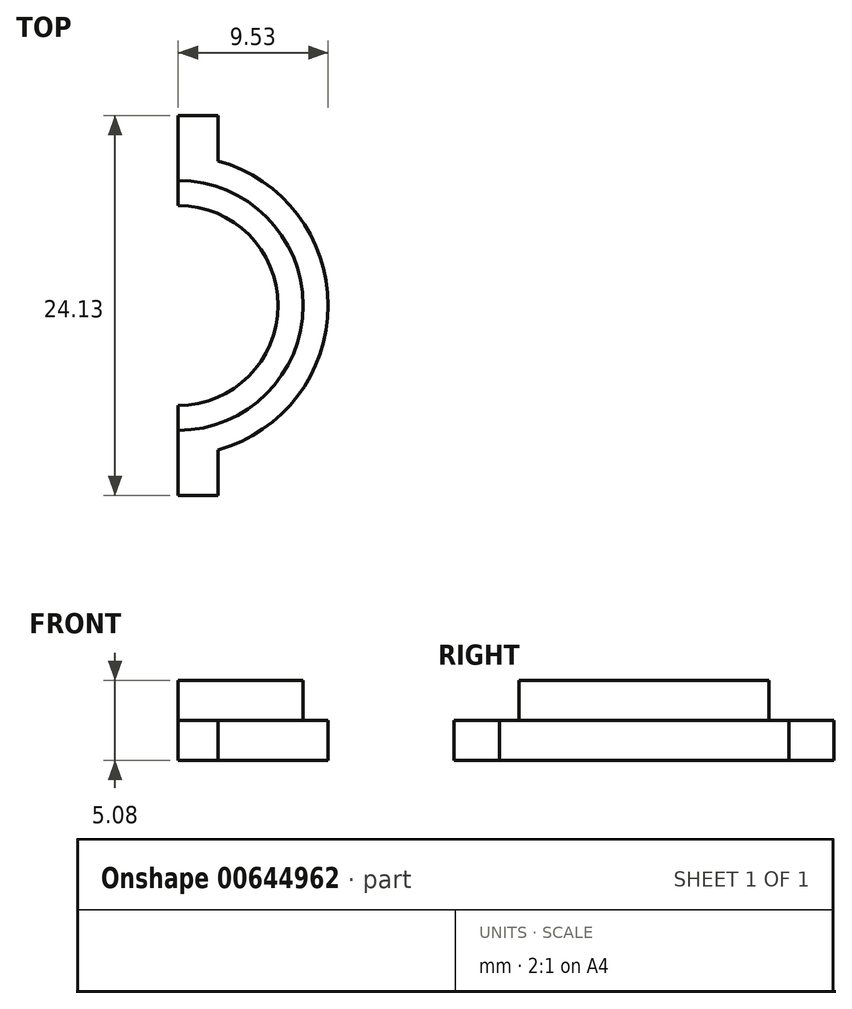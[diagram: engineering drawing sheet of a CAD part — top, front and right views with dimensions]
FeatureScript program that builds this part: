
annotation { "Feature Type Name" : "Feature", "Feature Type Description" : "" }
export const myFeature = defineFeature(function(context is Context, id is Id, definition is map)
    precondition{}
    {
        {
            var Q0;
            Q0=qCreatedBy(makeId("Top.planeOp"),FACE);
            var sketch = newSketch(context, id + "F0", { "sketchPlane" : qUnion([Q0])});
            skArc(sketch, "E0", {"start": v(0, 2.85) * mm, "mid": v(9.52, 12.38) * mm, "end": v(0, 21.9) * mm});
            skArc(sketch, "E1", {"start": v(0, 6.03) * mm, "mid": v(6.35, 12.38) * mm, "end": v(0, 18.73) * mm});
            skLineSegment(sketch, "E2", {"start": v(0, 2.85) * mm, "end": v(0, 6.03) * mm});
            skLineSegment(sketch, "E3.trimOffspring", {"start": v(0, 18.73) * mm, "end": v(0, 21.9) * mm});
            skLineSegment(sketch, "E4", {"start": v(0, 21.9) * mm, "end": v(0, 24.44) * mm});
            skLineSegment(sketch, "E5", {"start": v(2.54, 21.56) * mm, "end": v(2.54, 24.44) * mm});
            skLineSegment(sketch, "E6", {"start": v(0, 24.44) * mm, "end": v(2.54, 24.44) * mm});
            skLineSegment(sketch, "E7", {"start": v(0, 2.85) * mm, "end": v(0, 0.31) * mm});
            skLineSegment(sketch, "E8", {"start": v(0, 0.31) * mm, "end": v(2.54, 0.31) * mm});
            skLineSegment(sketch, "E9", {"start": v(2.54, 0.31) * mm, "end": v(2.54, 3.2) * mm});
            skSolve(sketch);
        }
        {
            var Q0;
            Q0 = qSketchRegion(id + "F0", true);
            extrude(context, id + "F1", {"entities" : qUnion([Q0]), "depth" : 2.54 * mm, "offsetDistance" : 25.4 * mm});
        }
        {
            var Q0;
            Q0=makeQuery(id+"F1.opExtrude","CAP_FACE",FACE,{"disambiguationData":[OSD([sQuery(id+"F0.wireOp",EDGE,"E0"),sQuery(id+"F0.wireOp",EDGE,"E1"),sQuery(id+"F0.wireOp",EDGE,"E2"),sQuery(id+"F0.wireOp",EDGE,"E3.trimOffspring"),sQuery(id+"F0.wireOp",EDGE,"E4"),sQuery(id+"F0.wireOp",EDGE,"E5"),sQuery(id+"F0.wireOp",EDGE,"E6"),sQuery(id+"F0.wireOp",EDGE,"E7"),sQuery(id+"F0.wireOp",EDGE,"E8"),sQuery(id+"F0.wireOp",EDGE,"E9")])],"isStart":false});
            var sketch = newSketch(context, id + "F2", { "sketchPlane" : qUnion([Q0])});
            skArc(sketch, "E10", {"start": v(0, 4.44) * mm, "mid": v(7.94, 12.38) * mm, "end": v(0, 20.32) * mm});
            skLineSegment(sketch, "E11", {"start": v(0, 18.73) * mm, "end": v(0, 20.32) * mm});
            skLineSegment(sketch, "E12", {"start": v(0, 20.32) * mm, "end": v(0, 18.73) * mm});
            skLineSegment(sketch, "E13", {"start": v(0, 6.03) * mm, "end": v(0, 4.44) * mm});
            skArc(sketch, "E14", {"start": v(0, 18.73) * mm, "mid": v(6.35, 12.38) * mm, "end": v(0, 6.03) * mm});
            skSolve(sketch);
        }
        {
            var Q0;
            Q0 = qSketchRegion(id + "F2", true);
            extrude(context, id + "F3", {"entities" : qUnion([Q0]), "operationType" : NewBodyOperationType.ADD, "depth" : 2.54 * mm, "offsetDistance" : 25.4 * mm});
        }
    });
